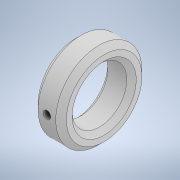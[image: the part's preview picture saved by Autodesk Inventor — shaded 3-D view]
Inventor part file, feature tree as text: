
AUTODESK INVENTOR PART (.ipt)
format: ipt  version: 2022 (Build 260153000, 153)  size: 144,896 bytes
history: native  units: mm
features: other x2, sketch x2, hole x1, projected_geometry x1, revolve x1
ambient origin geometry x8: Origin, YZ Plane, XZ Plane, XY Plane, X Axis, Y Axis, Z Axis, Center Point
bodies: Body1 (feature_tree)
feature tree (7):
  other  "Твердое тело1"
  other  "РабПлоскость1"
  hole  "Отверстие1"  [1 undecoded]
  sketch  "Эскиз2"
  projected_geometry  "Спроецированная петля1"
  sketch  "Эскиз1"
  revolve  "Вращение1"
note: 1 required parameter value undecoded (feature->parameter linkage not recoverable at this tier; creation-order binding heuristic only, values carry confidence <= 0.55)
